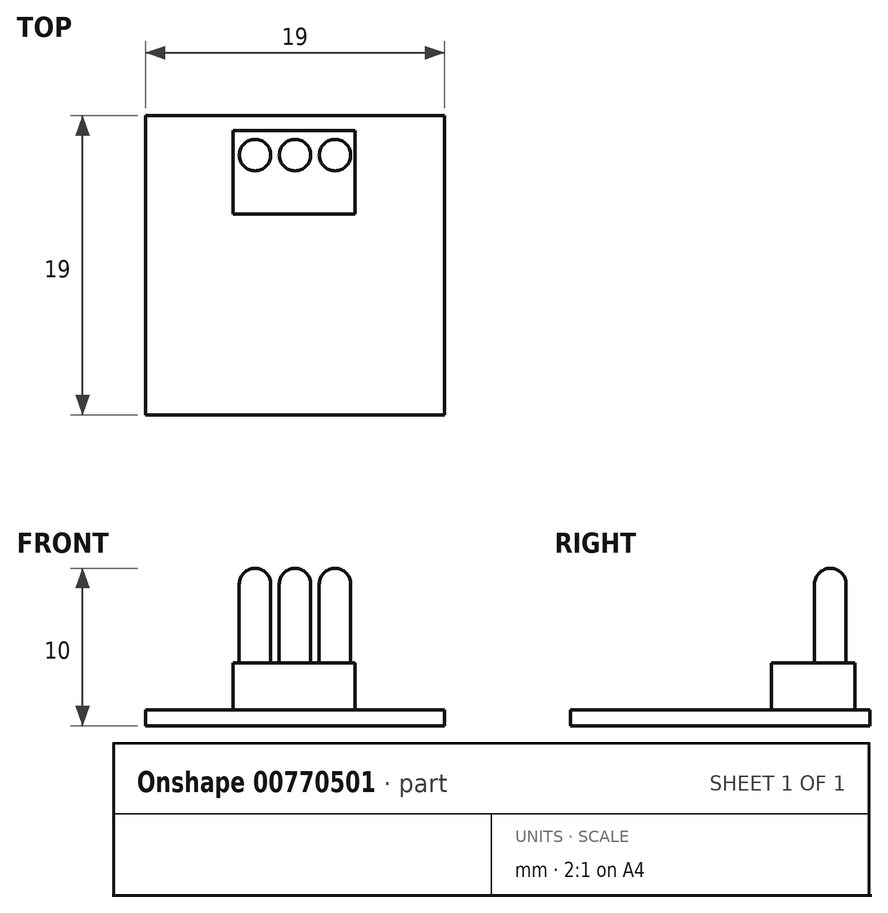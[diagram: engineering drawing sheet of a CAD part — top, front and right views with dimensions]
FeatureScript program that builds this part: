
annotation { "Feature Type Name" : "Feature", "Feature Type Description" : "" }
export const myFeature = defineFeature(function(context is Context, id is Id, definition is map)
    precondition{}
    {
        {
            var Q0;
            Q0=qCreatedBy(makeId("Top.planeOp"),FACE);
            var sketch = newSketch(context, id + "F0", { "sketchPlane" : qUnion([Q0])});
            skLineSegment(sketch, "E0.bottom", {"start": v(-9.5, 2.5) * mm, "end": v(9.5, 2.5) * mm});
            skLineSegment(sketch, "E0.top", {"start": v(-9.5, -16.5) * mm, "end": v(9.5, -16.5) * mm});
            skLineSegment(sketch, "E0.left", {"start": v(-9.5, 2.5) * mm, "end": v(-9.5, -16.5) * mm});
            skLineSegment(sketch, "E0.right", {"start": v(9.5, 2.5) * mm, "end": v(9.5, -16.5) * mm});
            skSolve(sketch);
        }
        {
            var Q0;
            Q0=makeQuery(id+"F0.imprint","IMPRINT",FACE,{"disambiguationData":[TD([[makeQuery(id+"F0.imprint","IMPRINT",EDGE,{"derivedFrom":sQuery(id+"F0.wireOp",EDGE,"E0.bottom")}),-1.0]])]});
            extrude(context, id + "F1", {"entities" : qUnion([Q0]), "depth" : 1 * mm, "offsetDistance" : 25 * mm});
        }
        {
            var Q0;
            Q0=makeQuery(id+"F1.opExtrude","CAP_FACE",FACE,{"disambiguationData":[OSD([sQuery(id+"F0.wireOp",EDGE,"E0.bottom"),sQuery(id+"F0.wireOp",EDGE,"E0.top"),sQuery(id+"F0.wireOp",EDGE,"E0.left"),sQuery(id+"F0.wireOp",EDGE,"E0.right")])],"isStart":false});
            var sketch = newSketch(context, id + "F2", { "sketchPlane" : qUnion([Q0])});
            skLineSegment(sketch, "E1.bottom", {"start": v(-3.94, 1.56) * mm, "end": v(3.8, 1.56) * mm});
            skLineSegment(sketch, "E1.top", {"start": v(-3.94, -3.73) * mm, "end": v(3.8, -3.73) * mm});
            skLineSegment(sketch, "E1.left", {"start": v(-3.94, 1.56) * mm, "end": v(-3.94, -3.73) * mm});
            skLineSegment(sketch, "E1.right", {"start": v(3.8, 1.56) * mm, "end": v(3.8, -3.73) * mm});
            skSolve(sketch);
        }
        {
            var Q0;
            Q0=makeQuery(id+"F2.imprint","IMPRINT",FACE,{"disambiguationData":[TD([[makeQuery(id+"F2.imprint","IMPRINT",EDGE,{"derivedFrom":sQuery(id+"F2.wireOp",EDGE,"E1.bottom")}),-1.0]])]});
            extrude(context, id + "F3", {"entities" : qUnion([Q0]), "depth" : 3 * mm, "offsetDistance" : 25 * mm});
        }
        {
            var Q0;
            Q0=makeQuery(id+"F3.opExtrude","CAP_FACE",FACE,{"disambiguationData":[OSD([sQuery(id+"F2.wireOp",EDGE,"E1.bottom"),sQuery(id+"F2.wireOp",EDGE,"E1.top"),sQuery(id+"F2.wireOp",EDGE,"E1.left"),sQuery(id+"F2.wireOp",EDGE,"E1.right")])],"isStart":false});
            var sketch = newSketch(context, id + "F4", { "sketchPlane" : qUnion([Q0])});
            skCircle(sketch, "E2", {"center": v(-2.54, 0) * mm, "radius": 1 * mm});
            skCircle(sketch, "E3", {"center": v(0, 0) * mm, "radius": 1 * mm});
            skCircle(sketch, "E4", {"center": v(2.54, 0) * mm, "radius": 1 * mm});
            skSolve(sketch);
        }
        {
            var Q0;
            Q0=makeQuery(id+"F4.imprint","IMPRINT",FACE,{"disambiguationData":[TD([[makeQuery(id+"F4.imprint","IMPRINT",EDGE,{"derivedFrom":sQuery(id+"F4.wireOp",EDGE,"E2")}),1.0]])]});
            var Q1;
            Q1=makeQuery(id+"F4.imprint","IMPRINT",FACE,{"disambiguationData":[TD([[makeQuery(id+"F4.imprint","IMPRINT",EDGE,{"derivedFrom":sQuery(id+"F4.wireOp",EDGE,"E3")}),1.0]])]});
            var Q2;
            Q2=makeQuery(id+"F4.imprint","IMPRINT",FACE,{"disambiguationData":[TD([[makeQuery(id+"F4.imprint","IMPRINT",EDGE,{"derivedFrom":sQuery(id+"F4.wireOp",EDGE,"E4")}),1.0]])]});
            extrude(context, id + "F5", {"entities" : qUnion([Q0, Q1, Q2]), "depth" : 5 * mm, "offsetDistance" : 25 * mm});
        }
        {
            var Q0;
            Q0=qCreatedBy(makeId("Front.planeOp"),FACE);
            var sketch = newSketch(context, id + "F6", { "sketchPlane" : qUnion([Q0])});
            skArc(sketch, "E5", {"start": v(1, 9) * mm, "mid": v(0, 10) * mm, "end": v(-1, 9) * mm});
            skLineSegment(sketch, "E6", {"start": v(-1, 9) * mm, "end": v(1, 9) * mm});
            skArc(sketch, "E7", {"start": v(-1.54, 9) * mm, "mid": v(-2.54, 10) * mm, "end": v(-3.54, 9) * mm});
            skArc(sketch, "E8", {"start": v(3.54, 9) * mm, "mid": v(2.54, 10) * mm, "end": v(1.54, 9) * mm});
            skLineSegment(sketch, "E9", {"start": v(-3.54, 9) * mm, "end": v(-1.54, 9) * mm});
            skLineSegment(sketch, "E10", {"start": v(1.54, 9) * mm, "end": v(3.54, 9) * mm});
            skSolve(sketch);
        }
        {
            var Q0;
            Q0=makeQuery(id+"F6.imprint","IMPRINT",FACE,{"disambiguationData":[TD([[makeQuery(id+"F6.imprint","IMPRINT",EDGE,{"derivedFrom":sQuery(id+"F6.wireOp",EDGE,"E5")}),1.0]])]});
            var Q1;
            Q1=makeQuery(id+"F6.imprint","IMPRINT",FACE,{"disambiguationData":[TD([[makeQuery(id+"F6.imprint","IMPRINT",EDGE,{"derivedFrom":sQuery(id+"F6.wireOp",EDGE,"E8")}),1.0]])]});
            var Q2;
            Q2=makeQuery(id+"F6.imprint","IMPRINT",FACE,{"disambiguationData":[TD([[makeQuery(id+"F6.imprint","IMPRINT",EDGE,{"derivedFrom":sQuery(id+"F6.wireOp",EDGE,"E7")}),1.0]])]});
            var Q3;
            Q3=sQuery(id+"F6.wireOp",EDGE,"E6");
            revolve(context, id + "F7", {"operationType" : NewBodyOperationType.ADD, "surfaceOperationType" : NewSurfaceOperationType.NEW, "entities" : qUnion([Q0, Q1, Q2]), "axis" : qUnion([Q3]), "revolveType" : RevolveType.FULL});
        }
    });
